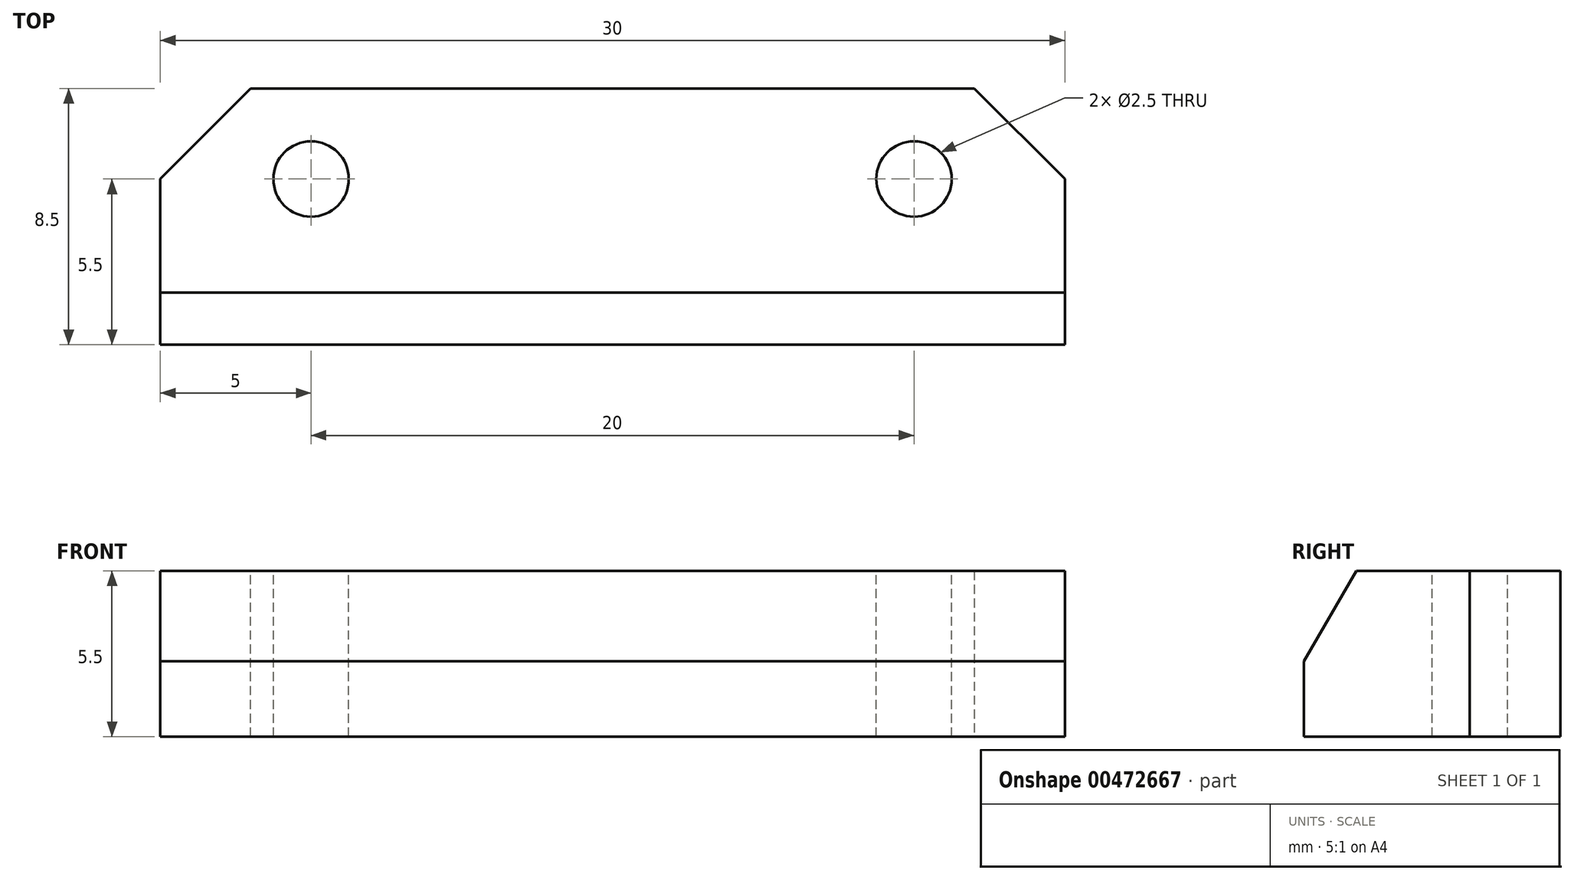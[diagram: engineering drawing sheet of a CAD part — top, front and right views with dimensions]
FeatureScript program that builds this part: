
annotation { "Feature Type Name" : "Feature", "Feature Type Description" : "" }
export const myFeature = defineFeature(function(context is Context, id is Id, definition is map)
    precondition{}
    {
        {
            var Q0;
            Q0=qCreatedBy(makeId("Front.planeOp"),FACE);
            var sketch = newSketch(context, id + "F0", { "sketchPlane" : qUnion([Q0])});
            skLineSegment(sketch, "E0.bottom", {"start": v(15, -2.75) * mm, "end": v(-15, -2.75) * mm});
            skLineSegment(sketch, "E0.top", {"start": v(15, 2.75) * mm, "end": v(-15, 2.75) * mm});
            skLineSegment(sketch, "E0.left", {"start": v(15, -2.75) * mm, "end": v(15, 2.75) * mm});
            skLineSegment(sketch, "E0.right", {"start": v(-15, -2.75) * mm, "end": v(-15, 2.75) * mm});
            skPoint(sketch, "E0.middle", {"position": v(0, 0) * mm});
            skSolve(sketch);
        }
        {
            var Q0;
            Q0 = qSketchRegion(id + "F0", true);
            extrude(context, id + "F1", {"entities" : qUnion([Q0]), "depth" : 8.5 * mm});
        }
        {
            var Q0;
            Q0=makeQuery(id+"F1.opExtrude","CAP_EDGE",EDGE,{"disambiguationData":[OSD([sQuery(id+"F0.wireOp",EDGE,"E0.right")])],"isStart":true});
            var Q1;
            Q1=makeQuery(id+"F1.opExtrude","CAP_EDGE",EDGE,{"disambiguationData":[OSD([sQuery(id+"F0.wireOp",EDGE,"E0.left")])],"isStart":true});
            chamfer(context, id + "F2", {"entities" : qUnion([Q0, Q1]), "width" : 3 * mm, "tangentPropagation" : true});
        }
        {
            var Q0;
            Q0=makeQuery(id+"F1.opExtrude","CAP_EDGE",EDGE,{"disambiguationData":[OSD([sQuery(id+"F0.wireOp",EDGE,"E0.top")])],"isStart":false});
            chamfer(context, id + "F3", {"entities" : qUnion([Q0]), "chamferType" : ChamferType.OFFSET_ANGLE, "width" : 3 * mm, "oppositeDirection" : false, "angle" : 30 * degree, "tangentPropagation" : true});
        }
        {
            var Q0;
            Q0=makeQuery(id+"F1.opExtrude","SWEPT_FACE",FACE,{"disambiguationData":[OSD([sQuery(id+"F0.wireOp",EDGE,"E0.top")])]});
            var sketch = newSketch(context, id + "F4", { "sketchPlane" : qUnion([Q0])});
            skLineSegment(sketch, "E1", {"start": v(0, 0) * mm, "end": v(0, -6.74) * mm, "construction": true});
            skPoint(sketch, "E2", {"position": v(-10, -3) * mm});
            skPoint(sketch, "E3.MirrorP", {"position": v(10, -3) * mm});
            skSolve(sketch);
        }
        {
            var Q0;
            Q0=sQuery(id+"F4.wireOp",VERTEX,"E2");
            var Q1;
            Q1=sQuery(id+"F4.wireOp",VERTEX,"E3.MirrorP");
            var Q2;
            Q2=makeQuery(id+"F1.opExtrude","SWEPT_BODY",BODY,{"disambiguationData":[OSD([sQuery(id+"F0.wireOp",EDGE,"E0.bottom"),sQuery(id+"F0.wireOp",EDGE,"E0.top"),sQuery(id+"F0.wireOp",EDGE,"E0.left"),sQuery(id+"F0.wireOp",EDGE,"E0.right")])]});
            hole(context, id + "F5", {"style" : HoleStyle.SIMPLE, "endStyle" : HoleEndStyle.THROUGH, "standardTappedOrClearance" : lookupTablePath({ "standard" : "ISO", "engagement" : "75%", "pitch" : "0.5 mm", "size" : "M3", "type" : "Tapped" }), "standardBlindInLast" : lookupTablePath({ "standard" : "ISO", "engagement" : "75%", "pitch" : "0.5 mm", "size" : "M3", "type" : "Tapped" }), "holeDiameter" : 2.5 * mm, "showTappedDepth" : true, "isTappedThrough" : true, "tappedDepth" : 6.2 * mm, "tapClearance" : 3, "locations" : qUnion([Q0, Q1]), "scope" : qUnion([Q2]), "majorDiameter" : 3 * mm});
        }
    });
